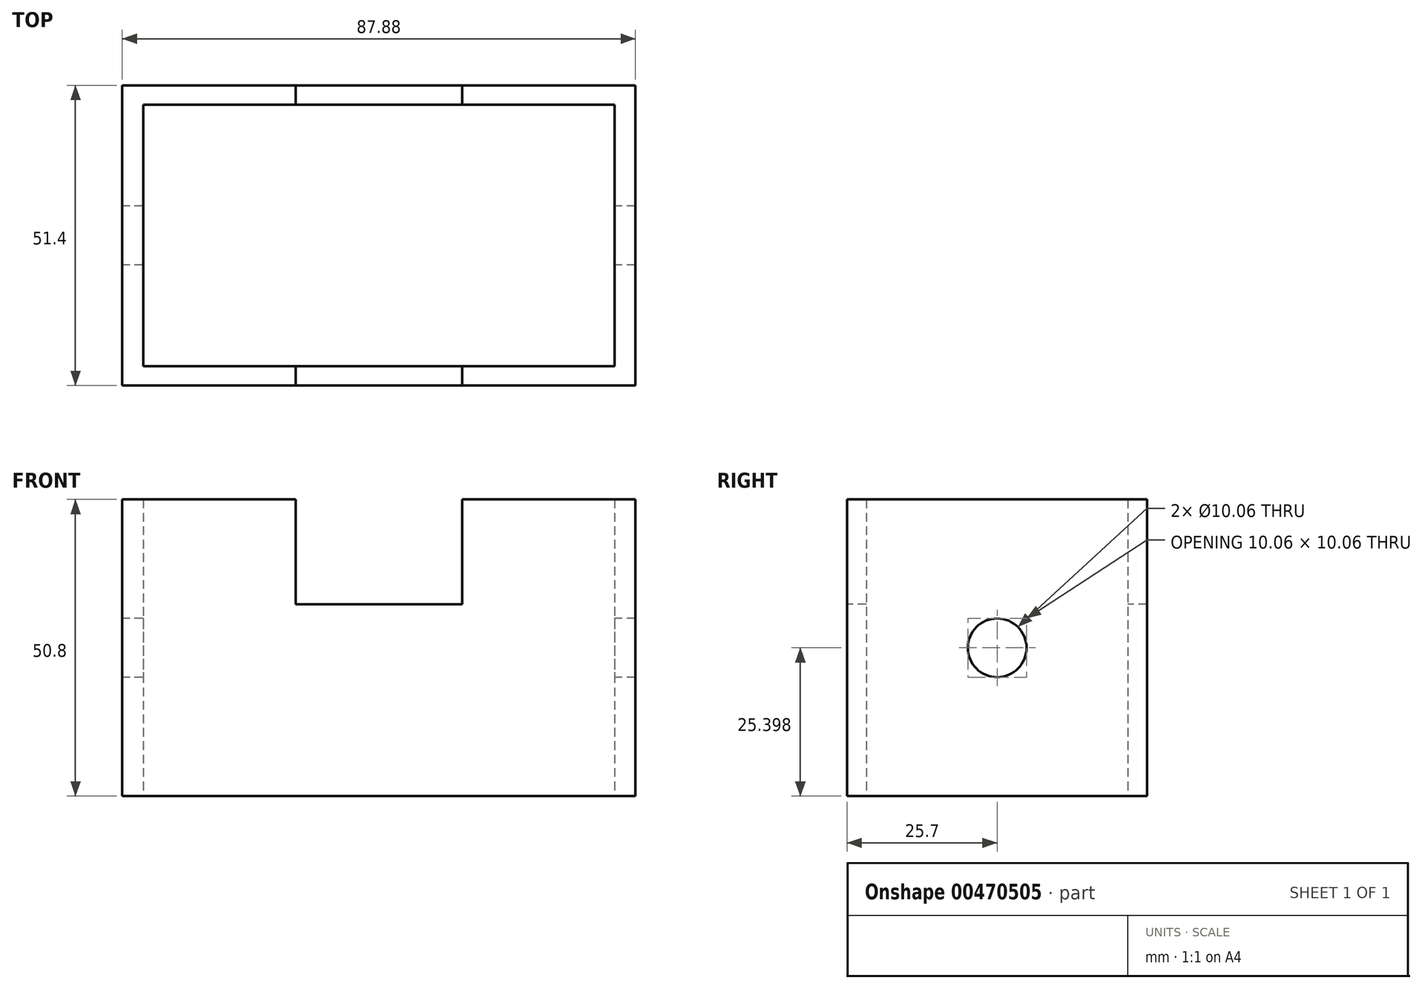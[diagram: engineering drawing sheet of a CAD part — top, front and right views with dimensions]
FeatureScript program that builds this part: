
annotation { "Feature Type Name" : "Feature", "Feature Type Description" : "" }
export const myFeature = defineFeature(function(context is Context, id is Id, definition is map)
    precondition{}
    {
        {
            var Q0;
            Q0=qCreatedBy(makeId("Right.planeOp"),FACE);
            var sketch = newSketch(context, id + "F0", { "sketchPlane" : qUnion([Q0])});
            skLineSegment(sketch, "E0.bottom", {"start": v(25.7, 0) * mm, "end": v(-25.7, 0) * mm});
            skLineSegment(sketch, "E0.top", {"start": v(25.7, 50.8) * mm, "end": v(-25.7, 50.8) * mm});
            skLineSegment(sketch, "E0.left", {"start": v(25.7, 0) * mm, "end": v(25.7, 50.8) * mm});
            skLineSegment(sketch, "E0.right", {"start": v(-25.7, 0) * mm, "end": v(-25.7, 50.8) * mm});
            skPoint(sketch, "E0.middle", {"position": v(0, 25.4) * mm});
            skCircle(sketch, "E1", {"center": v(0, 25.4) * mm, "radius": 5.03 * mm});
            skSolve(sketch);
        }
        {
            var Q0;
            Q0 = qSketchRegion(id + "F0", true);
            extrude(context, id + "F1", {"entities" : qUnion([Q0]), "endBound" : BoundingType.SYMMETRIC, "depth" : 87.88 * mm});
        }
        {
            var Q0;
            Q0=qCreatedBy(makeId("Front.planeOp"),FACE);
            var sketch = newSketch(context, id + "F2", { "sketchPlane" : qUnion([Q0])});
            skLineSegment(sketch, "E2.bottom", {"start": v(14.26, 32.83) * mm, "end": v(-14.26, 32.83) * mm});
            skLineSegment(sketch, "E2.top", {"start": v(14.26, 50.9) * mm, "end": v(-14.26, 50.9) * mm});
            skLineSegment(sketch, "E2.left", {"start": v(14.26, 32.83) * mm, "end": v(14.26, 50.9) * mm});
            skLineSegment(sketch, "E2.right", {"start": v(-14.26, 32.83) * mm, "end": v(-14.26, 50.9) * mm});
            skPoint(sketch, "E2.middle", {"position": v(0, 41.86) * mm});
            skSolve(sketch);
        }
        {
            var Q0;
            Q0 = qSketchRegion(id + "F2", true);
            extrude(context, id + "F3", {"entities" : qUnion([Q0]), "operationType" : NewBodyOperationType.REMOVE, "endBound" : BoundingType.SYMMETRIC, "oppositeDirection" : true, "depth" : 51.82 * mm});
        }
        {
            var Q0;
            Q0=qCreatedBy(makeId("Top.planeOp"),FACE);
            var sketch = newSketch(context, id + "F4", { "sketchPlane" : qUnion([Q0])});
            skLineSegment(sketch, "E3.bottom", {"start": v(40.36, -22.39) * mm, "end": v(-40.36, -22.39) * mm});
            skLineSegment(sketch, "E3.top", {"start": v(40.36, 22.39) * mm, "end": v(-40.36, 22.39) * mm});
            skLineSegment(sketch, "E3.left", {"start": v(40.36, -22.39) * mm, "end": v(40.36, 22.39) * mm});
            skLineSegment(sketch, "E3.right", {"start": v(-40.36, -22.39) * mm, "end": v(-40.36, 22.39) * mm});
            skPoint(sketch, "E3.middle", {"position": v(0, 0) * mm});
            skSolve(sketch);
        }
        {
            var Q0;
            Q0 = qSketchRegion(id + "F4", true);
            extrude(context, id + "F5", {"entities" : qUnion([Q0]), "operationType" : NewBodyOperationType.REMOVE, "depth" : 84.84 * mm});
        }
    });
